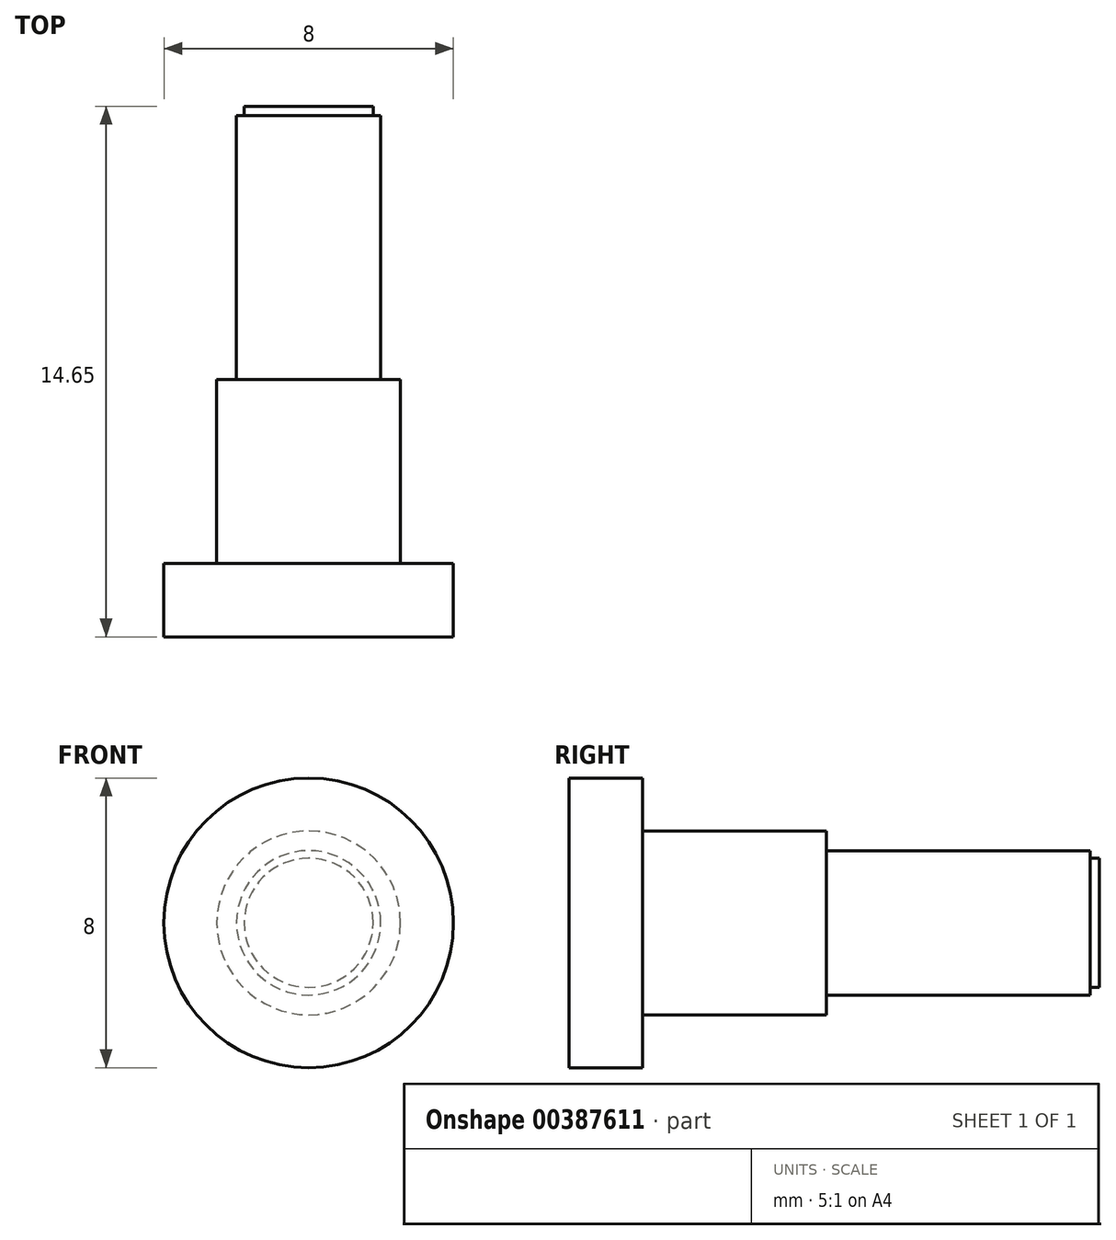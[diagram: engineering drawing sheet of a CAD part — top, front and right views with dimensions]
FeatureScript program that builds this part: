
annotation { "Feature Type Name" : "Feature", "Feature Type Description" : "" }
export const myFeature = defineFeature(function(context is Context, id is Id, definition is map)
    precondition{}
    {
        {
            var Q0;
            Q0=qCreatedBy(makeId("Front.planeOp"),FACE);
            var sketch = newSketch(context, id + "F0", { "sketchPlane" : qUnion([Q0])});
            skCircle(sketch, "E0", {"center": v(0, 0) * mm, "radius": 4 * mm});
            skCircle(sketch, "E1", {"center": v(0, 0) * mm, "radius": 3 * mm});
            skSolve(sketch);
        }
        {
            var Q0;
            Q0=makeQuery(id+"F0.imprint","IMPRINT",FACE,{"disambiguationData":[TD([[makeQuery(id+"F0.imprint","IMPRINT",EDGE,{"derivedFrom":sQuery(id+"F0.wireOp",EDGE,"E0")}),1.0]])]});
            var Q1;
            Q1=makeQuery(id+"F0.imprint","IMPRINT",FACE,{"disambiguationData":[TD([[makeQuery(id+"F0.imprint","IMPRINT",EDGE,{"derivedFrom":sQuery(id+"F0.wireOp",EDGE,"E1")}),1.0]])]});
            extrude(context, id + "F1", {"entities" : qUnion([Q0, Q1]), "depth" : 2.03 * mm});
        }
        {
            var Q0;
            Q0=makeQuery(id+"F1.opExtrude","CAP_FACE",FACE,{"disambiguationData":[OSD([sQuery(id+"F0.wireOp",EDGE,"E0")])],"isStart":true});
            var sketch = newSketch(context, id + "F2", { "sketchPlane" : qUnion([Q0])});
            skCircle(sketch, "E2", {"center": v(0, 0) * mm, "radius": 2.54 * mm});
            skSolve(sketch);
        }
        {
            var Q0;
            Q0=makeQuery(id+"F2.imprint","IMPRINT",FACE,{"disambiguationData":[TD([[makeQuery(id+"F2.imprint","IMPRINT",EDGE,{"derivedFrom":sQuery(id+"F2.wireOp",EDGE,"E2")}),1.0]])]});
            extrude(context, id + "F3", {"entities" : qUnion([Q0]), "operationType" : NewBodyOperationType.ADD, "depth" : 5.08 * mm});
        }
        {
            var Q0;
            Q0=makeQuery(id+"F3.opExtrude","CAP_FACE",FACE,{"disambiguationData":[OSD([sQuery(id+"F2.wireOp",EDGE,"E2")])],"isStart":false});
            var sketch = newSketch(context, id + "F4", { "sketchPlane" : qUnion([Q0])});
            skCircle(sketch, "E3", {"center": v(0, 0) * mm, "radius": 2 * mm});
            skSolve(sketch);
        }
        {
            var Q0;
            Q0=makeQuery(id+"F4.imprint","IMPRINT",FACE,{"disambiguationData":[TD([[makeQuery(id+"F4.imprint","IMPRINT",EDGE,{"derivedFrom":sQuery(id+"F4.wireOp",EDGE,"E3")}),1.0]])]});
            extrude(context, id + "F5", {"entities" : qUnion([Q0]), "operationType" : NewBodyOperationType.ADD, "depth" : 7.3 * mm});
        }
        {
            var Q0;
            Q0=makeQuery(id+"F5.opExtrude","CAP_FACE",FACE,{"disambiguationData":[OSD([sQuery(id+"F4.wireOp",EDGE,"E3")])],"isStart":false});
            var sketch = newSketch(context, id + "F6", { "sketchPlane" : qUnion([Q0])});
            skCircle(sketch, "E4", {"center": v(0, 0) * mm, "radius": 1.78 * mm});
            skSolve(sketch);
        }
        {
            var Q0;
            Q0=qSketchRegion(id+"F6",true);
            extrude(context, id + "F7", {"entities" : qUnion([Q0]), "operationType" : NewBodyOperationType.ADD, "depth" : 0.25 * mm});
        }
    });
